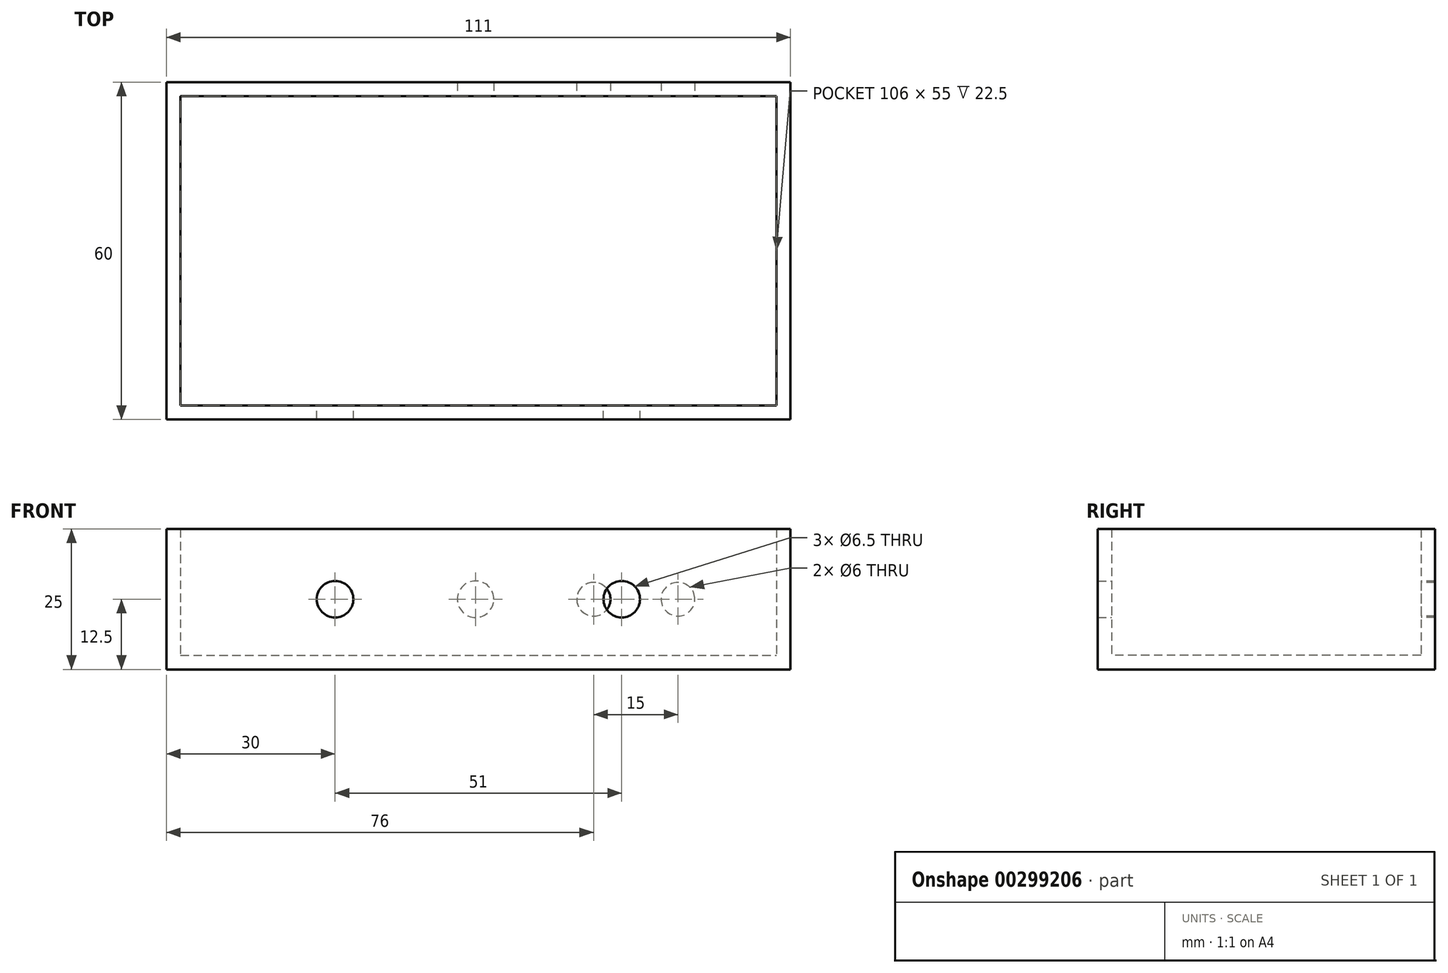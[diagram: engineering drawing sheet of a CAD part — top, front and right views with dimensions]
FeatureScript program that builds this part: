
annotation { "Feature Type Name" : "Feature", "Feature Type Description" : "" }
export const myFeature = defineFeature(function(context is Context, id is Id, definition is map)
    precondition{}
    {
        {
            var Q0;
            Q0=qCreatedBy(makeId("Top.planeOp"),FACE);
            var sketch = newSketch(context, id + "F0", { "sketchPlane" : qUnion([Q0])});
            skLineSegment(sketch, "E0.bottom", {"start": v(-55.5, 30) * mm, "end": v(55.5, 30) * mm});
            skLineSegment(sketch, "E0.top", {"start": v(-55.5, -30) * mm, "end": v(55.5, -30) * mm});
            skLineSegment(sketch, "E0.left", {"start": v(-55.5, 30) * mm, "end": v(-55.5, -30) * mm});
            skLineSegment(sketch, "E0.right", {"start": v(55.5, 30) * mm, "end": v(55.5, -30) * mm});
            skPoint(sketch, "E0.middle", {"position": v(0, 0) * mm});
            skSolve(sketch);
        }
        {
            var Q0;
            Q0 = qSketchRegion(id + "F0", true);
            extrude(context, id + "F1", {"entities" : qUnion([Q0]), "depth" : 25 * mm, "offsetDistance" : 25 * mm});
        }
        {
            var Q0;
            Q0=makeQuery(id+"F1.opExtrude","CAP_FACE",FACE,{"disambiguationData":[OSD([sQuery(id+"F0.wireOp",EDGE,"E0.bottom"),sQuery(id+"F0.wireOp",EDGE,"E0.top"),sQuery(id+"F0.wireOp",EDGE,"E0.left"),sQuery(id+"F0.wireOp",EDGE,"E0.right")])],"isStart":false});
            shell(context, id + "F2", {"entities" : qUnion([Q0]), "thickness" : 2.5 * mm});
        }
        {
            var Q0;
            Q0=qCreatedBy(makeId("Front.planeOp"),FACE);
            var sketch = newSketch(context, id + "F3", { "sketchPlane" : qUnion([Q0])});
            skCircle(sketch, "E1", {"center": v(-25.5, 12.5) * mm, "radius": 3.25 * mm});
            skCircle(sketch, "E2", {"center": v(25.5, 12.5) * mm, "radius": 3.25 * mm});
            skSolve(sketch);
        }
        {
            var Q0;
            Q0 = qSketchRegion(id + "F3", true);
            var Q1;
            Q1=makeQuery(id+"F1.opExtrude","SWEPT_FACE",FACE,{"disambiguationData":[OSD([sQuery(id+"F0.wireOp",EDGE,"E0.top")])]});
            extrude(context, id + "F4", {"entities" : qUnion([Q0]), "operationType" : NewBodyOperationType.REMOVE, "endBound" : BoundingType.UP_TO_SURFACE, "endBoundEntityFace" : qUnion([Q1]), "depth" : 25 * mm});
        }
        {
            var Q0;
            Q0=qCreatedBy(makeId("Front.planeOp"),FACE);
            var sketch = newSketch(context, id + "F5", { "sketchPlane" : qUnion([Q0])});
            skCircle(sketch, "E3", {"center": v(-0.5, 12.5) * mm, "radius": 3.25 * mm});
            skCircle(sketch, "E4", {"center": v(20.5, 12.5) * mm, "radius": 3 * mm});
            skCircle(sketch, "E5", {"center": v(35.5, 12.5) * mm, "radius": 3 * mm});
            skSolve(sketch);
        }
        {
            var Q0;
            Q0 = qSketchRegion(id + "F5", true);
            var Q1;
            Q1=sQuery(id+"F3.wireOp",EDGE,"6b3c8190-12d1-4cdc-be77-9b485b5c09c6");
            var Q2;
            Q2=makeQuery(id+"F1.opExtrude","SWEPT_FACE",FACE,{"disambiguationData":[OSD([sQuery(id+"F0.wireOp",EDGE,"E0.bottom")])]});
            extrude(context, id + "F6", {"entities" : qUnion([Q0]), "operationType" : NewBodyOperationType.REMOVE, "surfaceEntities" : qUnion([Q1]), "endBound" : BoundingType.UP_TO_SURFACE, "oppositeDirection" : true, "endBoundEntityFace" : qUnion([Q2]), "depth" : 25 * mm, "offsetDistance" : 25 * mm});
        }
    });
